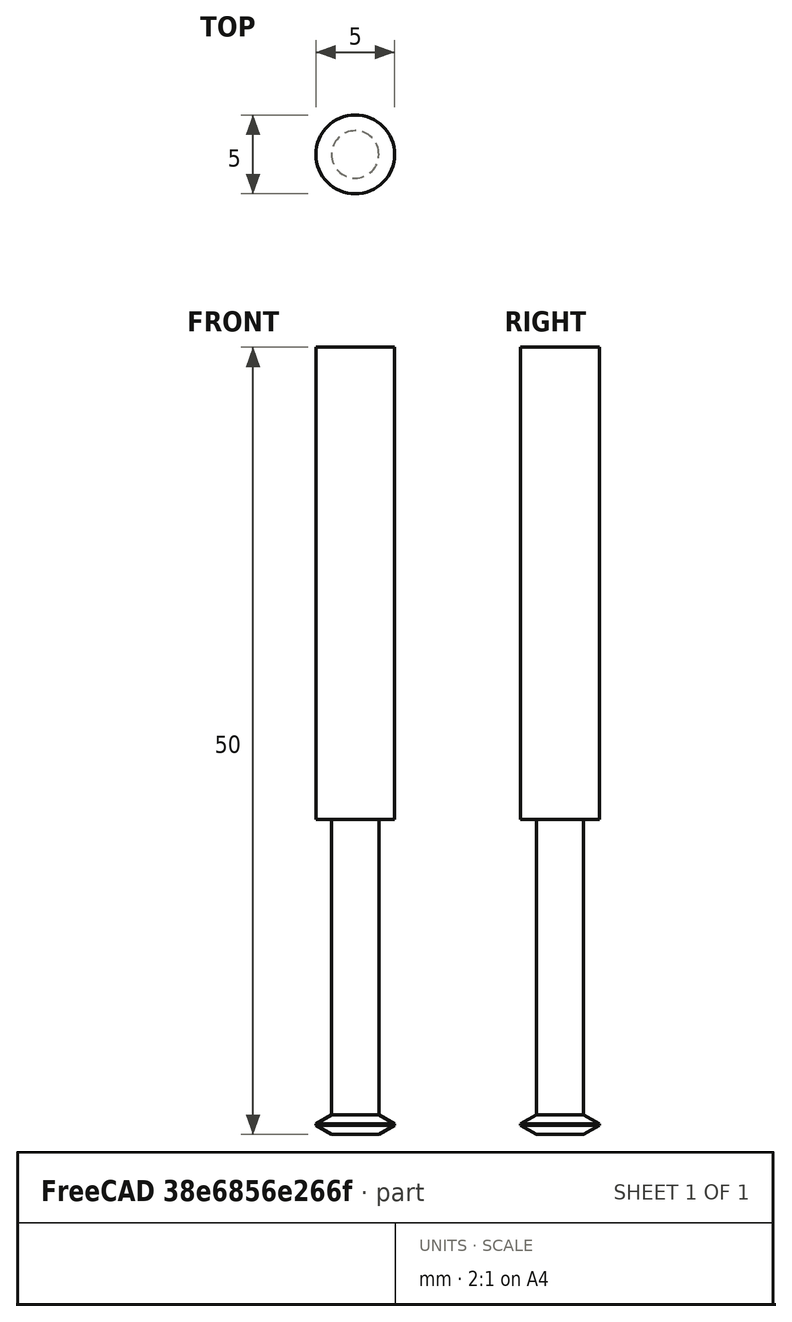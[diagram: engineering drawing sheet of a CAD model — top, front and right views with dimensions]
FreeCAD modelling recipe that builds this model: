
FCSTD DOCUMENT  (FreeCAD 0.19R24049 (Git))
Label: thread-mill
License: All rights reserved
LicenseURL: http://en.wikipedia.org/wiki/All_rights_reserved
objects: Sketcher::SketchObject×1, PartDesign::Revolution×1, App::FeaturePython×1, PartDesign::Body×1
note: 4 computed .brp shape members not serialized (recipe doc carries the construction recipe); baked Part::Feature solids carry a one-line shape summary decoded from their .brp

FEATURE [Sketcher::SketchObject] Sketch
  FullyConstrained = true
  MapMode = 5
  Placement = pos=(0,0,0) rot=(1,0,0;1.5708rad)
  Support = -> [XZ_Plane]
  expr: Constraints[8] = <<Attributes>>.ShankDiameter
  expr: Constraints[27] = <<Attributes>>.NeckLength
  expr: Constraints[30] = <<Attributes>>.NeckDiameter
  expr: Constraints[21] = <<Attributes>>.Crest
  expr: Constraints[5] = <<Attributes>>.Length
  expr: Constraints[18] = <<Attributes>>.Diameter
  expr: Constraints[19] = <<Attributes>>.cuttingAngle
  expr: Constraints[15] = <<Attributes>>.cuttingAngle
  sketch-geometry (12):
    g0: LineSegment StartX=0 StartY=50 StartZ=0 EndX=0 EndY=0 EndZ=0
    g1: LineSegment StartX=0 StartY=0 StartZ=0 EndX=1.5 EndY=0 EndZ=0
    g2: LineSegment StartX=2.5 StartY=50 StartZ=0 EndX=0 EndY=50 EndZ=0
    g3: LineSegment StartX=1.5 StartY=1.2547 StartZ=0 EndX=2.5 EndY=0.67735 EndZ=0
    g4: LineSegment StartX=1.5 StartY=20 StartZ=0 EndX=1.5 EndY=1.2547 EndZ=0
    g5: LineSegment StartX=-2.5 StartY=50 StartZ=0 EndX=2.5 EndY=50 EndZ=0
    g6: LineSegment StartX=2.5 StartY=0.67735 StartZ=0 EndX=2.5 EndY=0.57735 EndZ=0
    g7: LineSegment StartX=2.5 StartY=0.57735 StartZ=0 EndX=1.5 EndY=0 EndZ=0
    g8: LineSegment StartX=2.5 StartY=0.57735 StartZ=0 EndX=-2.5 EndY=0.57735 EndZ=0
    g9: LineSegment StartX=2.5 StartY=50 StartZ=0 EndX=2.5 EndY=20.01 EndZ=0
    g10: LineSegment StartX=2.5 StartY=20.01 StartZ=0 EndX=1.5 EndY=20 EndZ=0
    g11: LineSegment StartX=1.5 StartY=20 StartZ=0 EndX=-1.5 EndY=20 EndZ=0
  constraints (32):
    c: Vertical(g0)
    c: Coincident(g0,g1)
    c: Horizontal(g1)
    c: Horizontal(g2)
    c: Coincident(g0,g2)
    c: DistanceY(g1,g2) = 50
    c: Vertical(g4)
    c: Symmetric(g5,g5,g0)
    c: DistanceX(g5,g5) = 5
    c: Coincident(g3,g4)
    c: Coincident(g0,g-1)
    c: Coincident(g6,g3)
    c: Vertical(g6)
    c: Coincident(g7,g6)
    c: Coincident(g7,g1)
    c: Angle(g3,g7) = 1.0472
    c: Coincident(g8,g6)
    c: Symmetric(g6,g8,g-2)
    c: DistanceX(g8,g8) = 5
    c: Angle(g-2,g3) = 1.0472
    c: Vertical(g1,g3)
    c: DistanceY(g6,g6) = 0.1
    c: Coincident(g5,g2)
    c: Coincident(g2,g9)
    c: Vertical(g9)
    c: Coincident(g9,g10)
    c: Coincident(g10,g4)
    c: DistanceY(g4) = 20
    c: Coincident(g11,g4)
    c: Symmetric(g4,g11,g0)
    c: DistanceX(g11,g11) = 3
    c: DistanceY(g4,g9) = 0.01
FEATURE [PartDesign::Revolution] Revolution
  AllowMultiFace = false
  Angle = 360
  Axis = (0,-2e-16,1)
  Base = (0,0,0)
  Placement = pos=(0,0,0) rot=(1,0,0;1.5708rad)
  Profile = -> Sketch
  ReferenceAxis = -> Sketch [V_Axis]
  Reversed = true
FEATURE [App::FeaturePython] PropertyBag  label="Attributes"  # WARN: FeaturePython — macro-defined, semantics opaque (R4)
  Chipload = 0
  Crest = 0.1
  CustomPropertyGroups = Attributes | Shape
  Diameter = 5
  Flutes = 0
  Length = 50
  Material = 0
  NeckDiameter = 3
  NeckLength = 20
  ShankDiameter = 5
  cuttingAngle = 60
FEATURE [PartDesign::Body] Body  label="ThreadMill"
  Group = -> [Sketch,Revolution,PropertyBag]
  Origin = -> Origin
  Tip = -> Revolution
